# Revit family: Wedge_CB-55_BIM
name_source: partatom
category: Arredi
units: mm (PartAtom-declared; Revit-internal decimal feet)

## family parameters
Attiva taglio nelle viste = No
Basato su piano di lavoro = No
Condiviso = No
Numero OmniClass = 23.40.20.00
Origine composizione di rendering = Geometria famiglia
Punto di calcolo locali = No
Sempre verticale = Sì
Taglio con vuoti quando caricato = No
Titolo OmniClass = General Furniture and Specialties

## types (1)
- CB-55
    AVAILABLE FINISHES = Ebonized black lacquer on Ash (EB) or bleached, white pigment, matte acrylic on Ash (BL). Raw effect lacquer on Oak (RE). Hand rubbed natural oil on Oak or Walnut (NA), or hand rubbed black oil on Walnut (BO).
    BASE MATERIAL = BASSAM_FELLOWS_COMFORT_LEATHER_02067_BEIGE
    BIM BADGE = https://bim.archiproducts.com
    COLLECTION = Wedge
    DEPTH = 613 mm
    Descrizione = Solid wood and upholstered chair with armrests
    HEIGHT = 771 mm
    MATERIAL DESCRIPTION = Solid wood. Steel support for armrests and backrest. Foam upholstery with single topstitch.
    Modello = Wedge Chair
    PRODUCT CODE = CB-55
    PRODUCT SHEET = https://www.archiproducts.com
    Produttore = BassamFellows
    Prospetto di default = 0 mm  [stored 0 ft]
    SEAT HEIGHT = 460 mm
    STRUCTURE MATERIAL = BASSAM_FELLOWS_TEAK_T-NA
    TECHNICAL SHEET = https://bassamfellows.com
    URL = https://bassamfellows.com
    WIDTH = 634 mm

note: [stored X ft] marks values corroborated as IEEE doubles in the binary element streams (Revit-internal decimal feet)

## geometry (parser evidence)
native form markers: Sweep x1
no freeform markers — native parametric forms only
